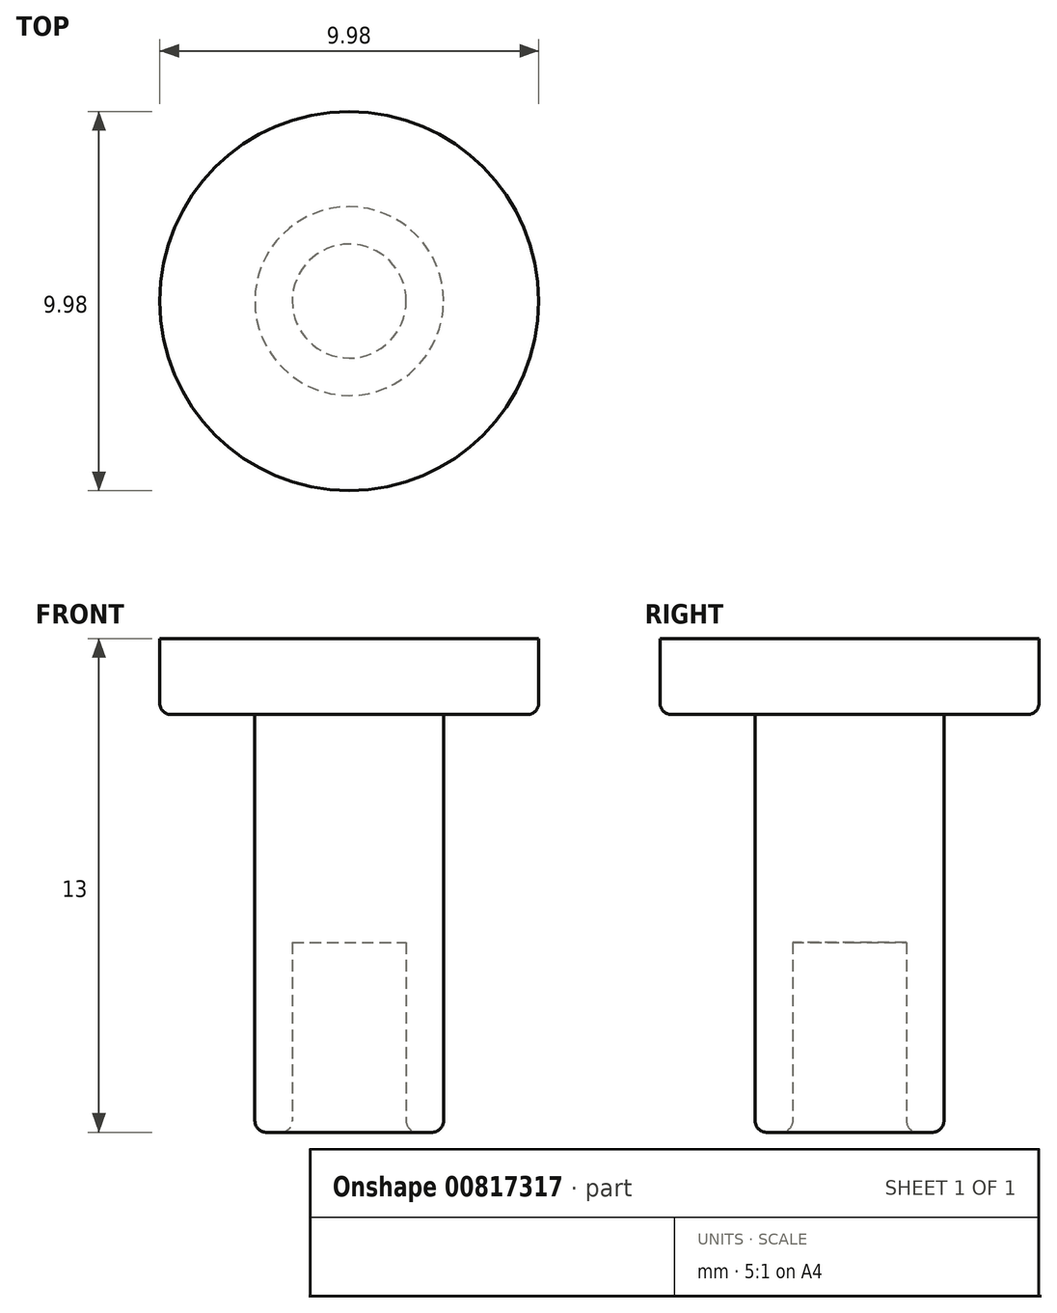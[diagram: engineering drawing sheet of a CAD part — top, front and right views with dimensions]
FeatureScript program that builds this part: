
annotation { "Feature Type Name" : "Feature", "Feature Type Description" : "" }
export const myFeature = defineFeature(function(context is Context, id is Id, definition is map)
    precondition{}
    {
        {
            var Q0;
            Q0=qCreatedBy(makeId("Top.planeOp"),FACE);
            var sketch = newSketch(context, id + "F0", { "sketchPlane" : qUnion([Q0])});
            skCircle(sketch, "E0", {"center": v(0, 0) * mm, "radius": 5 * mm});
            skSolve(sketch);
        }
        {
            var Q0;
            Q0 = qSketchRegion(id + "F0", true);
            extrude(context, id + "F1", {"entities" : qUnion([Q0]), "depth" : 2 * mm, "offsetDistance" : 25 * mm});
        }
        {
            var Q0;
            Q0=makeQuery(id+"F1.opExtrude","CAP_FACE",FACE,{"disambiguationData":[OSD([sQuery(id+"F0.wireOp",EDGE,"E0")])],"isStart":true});
            var sketch = newSketch(context, id + "F2", { "sketchPlane" : qUnion([Q0])});
            skCircle(sketch, "E1", {"center": v(0, 0) * mm, "radius": 2.48 * mm});
            skSolve(sketch);
        }
        {
            var Q0;
            Q0=makeQuery(id+"F2.imprint","IMPRINT",FACE,{"disambiguationData":[TD([[makeQuery(id+"F2.imprint","IMPRINT",EDGE,{"derivedFrom":sQuery(id+"F2.wireOp",EDGE,"E1")}),1.0]])]});
            extrude(context, id + "F3", {"entities" : qUnion([Q0]), "operationType" : NewBodyOperationType.ADD, "depth" : 11 * mm, "offsetDistance" : 25 * mm});
        }
        {
            var Q0;
            Q0=makeQuery(id+"F3.opExtrude","CAP_FACE",FACE,{"disambiguationData":[OSD([sQuery(id+"F2.wireOp",EDGE,"E1")])],"isStart":false});
            var sketch = newSketch(context, id + "F4", { "sketchPlane" : qUnion([Q0])});
            skCircle(sketch, "E2", {"center": v(0, 0) * mm, "radius": 1.5 * mm});
            skSolve(sketch);
        }
        {
            var Q0;
            Q0=makeQuery(id+"F4.imprint","IMPRINT",FACE,{"disambiguationData":[TD([[makeQuery(id+"F4.imprint","IMPRINT",EDGE,{"derivedFrom":sQuery(id+"F4.wireOp",EDGE,"E2")}),1.0]])]});
            extrude(context, id + "F5", {"entities" : qUnion([Q0]), "operationType" : NewBodyOperationType.REMOVE, "oppositeDirection" : true, "depth" : 5 * mm, "offsetDistance" : 25 * mm});
        }
        {
            var Q0;
            Q0=makeQuery(id+"F3.opExtrude","CAP_FACE",FACE,{"disambiguationData":[OSD([sQuery(id+"F2.wireOp",EDGE,"E1")])],"isStart":false});
            var Q1;
            Q1=makeQuery(id+"F1.opExtrude","CAP_EDGE",EDGE,{"disambiguationData":[OSD([sQuery(id+"F0.wireOp",EDGE,"E0")])],"isStart":true});
            fillet(context, id + "F6", {"entities" : qUnion([Q0, Q1]), "radius" : .3 * mm, "tangentPropagation" : true, "allowEdgeOverflow" : false});
        }
    });
